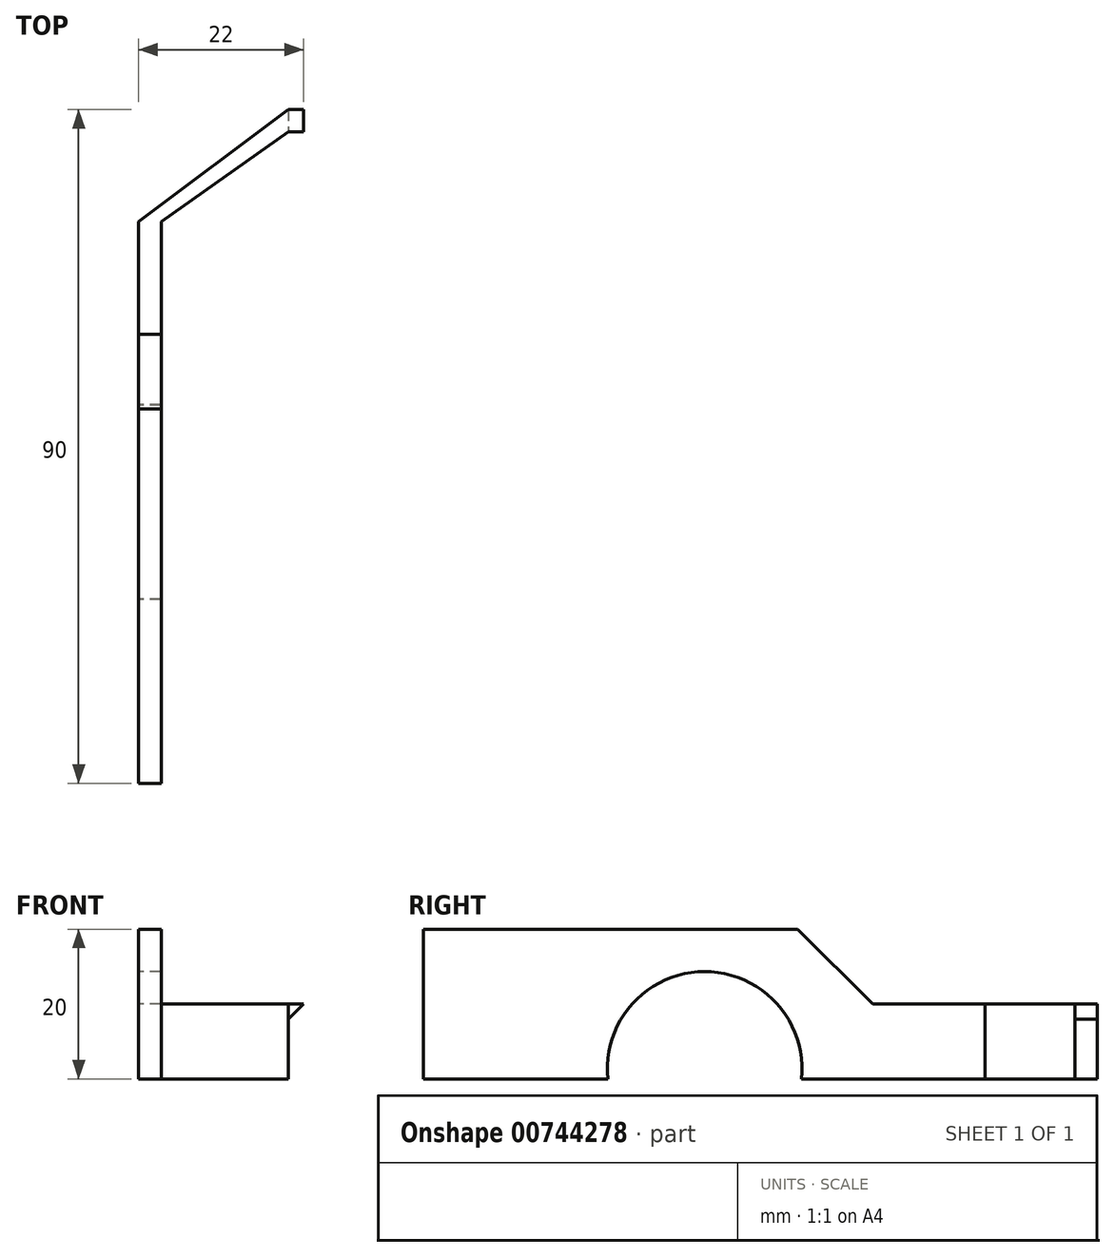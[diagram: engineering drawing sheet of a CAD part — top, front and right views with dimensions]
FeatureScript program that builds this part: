
annotation { "Feature Type Name" : "Feature", "Feature Type Description" : "" }
export const myFeature = defineFeature(function(context is Context, id is Id, definition is map)
    precondition{}
    {
        {
            var Q0;
            Q0=qCreatedBy(makeId("Top.planeOp"),FACE);
            var sketch = newSketch(context, id + "F0", { "sketchPlane" : qUnion([Q0])});
            skLineSegment(sketch, "E0", {"start": v(0, 0) * mm, "end": v(0, -3) * mm});
            skLineSegment(sketch, "E1", {"start": v(0, -3) * mm, "end": v(17, -15) * mm});
            skLineSegment(sketch, "E2", {"start": v(17, -15) * mm, "end": v(17, -90) * mm});
            skLineSegment(sketch, "E3", {"start": v(17, -90) * mm, "end": v(20, -90) * mm});
            skLineSegment(sketch, "E4", {"start": v(20, -90) * mm, "end": v(20, -15) * mm});
            skLineSegment(sketch, "E5", {"start": v(20, -15) * mm, "end": v(0, 0) * mm});
            skSolve(sketch);
        }
        {
            var Q0;
            Q0=qSketchRegion(id+"F0",true);
            extrude(context, id + "F1", {"entities" : qUnion([Q0]), "depth" : 10 * mm, "offsetDistance" : 25 * mm});
        }
        {
            var Q0;
            Q0=qCreatedBy(makeId("Front.planeOp"),FACE);
            var sketch = newSketch(context, id + "F2", { "sketchPlane" : qUnion([Q0])});
            skLineSegment(sketch, "E6", {"start": v(0, 10) * mm, "end": v(-2, 10) * mm});
            skLineSegment(sketch, "E7", {"start": v(-2, 10) * mm, "end": v(0, 8) * mm});
            skLineSegment(sketch, "E8", {"start": v(0, 8) * mm, "end": v(0, 10) * mm});
            skSolve(sketch);
        }
        {
            var Q0;
            Q0=qSketchRegion(id+"F2",true);
            extrude(context, id + "F3", {"entities" : qUnion([Q0]), "operationType" : NewBodyOperationType.ADD, "depth" : 3 * mm, "offsetDistance" : 25 * mm});
        }
        {
            var Q0;
            Q0=makeQuery(id+"F3.boolean.opBoolean","MERGE",FACE,{"derivedFrom":[makeQuery(id+"F1.opExtrude","CAP_FACE",FACE,{"disambiguationData":[OSD([sQuery(id+"F0.wireOp",EDGE,"E0"),sQuery(id+"F0.wireOp",EDGE,"E1"),sQuery(id+"F0.wireOp",EDGE,"E2"),sQuery(id+"F0.wireOp",EDGE,"E3"),sQuery(id+"F0.wireOp",EDGE,"E4"),sQuery(id+"F0.wireOp",EDGE,"E5")])],"isStart":false}),makeQuery(id+"F3.opExtrude","SWEPT_FACE",FACE,{"disambiguationData":[OSD([sQuery(id+"F2.wireOp",EDGE,"E6")])]})]});
            var sketch = newSketch(context, id + "F4", { "sketchPlane" : qUnion([Q0])});
            skLineSegment(sketch, "E9.bottom", {"start": v(17, -30) * mm, "end": v(20, -30) * mm});
            skLineSegment(sketch, "E9.top", {"start": v(17, -90) * mm, "end": v(20, -90) * mm});
            skLineSegment(sketch, "E9.left", {"start": v(17, -30) * mm, "end": v(17, -90) * mm});
            skLineSegment(sketch, "E9.right", {"start": v(20, -30) * mm, "end": v(20, -90) * mm});
            skSolve(sketch);
        }
        {
            var Q0;
            Q0=qSketchRegion(id+"F4",true);
            extrude(context, id + "F5", {"entities" : qUnion([Q0]), "operationType" : NewBodyOperationType.ADD, "depth" : 10 * mm, "offsetDistance" : 25 * mm});
        }
        {
            var Q0;
            Q0=makeQuery(id+"F5.opExtrude","CAP_EDGE",EDGE,{"disambiguationData":[OSD([sQuery(id+"F4.wireOp",EDGE,"E9.bottom")])],"isStart":false});
            chamfer(context, id + "F6", {"entities" : qUnion([Q0]), "width" : 10 * mm, "tangentPropagation" : true});
        }
        {
            var Q0;
            Q0=makeQuery(id+"F5.boolean.opBoolean","MERGE",FACE,{"derivedFrom":[makeQuery(id+"F1.opExtrude","SWEPT_FACE",FACE,{"disambiguationData":[OSD([sQuery(id+"F0.wireOp",EDGE,"E4")])]}),makeQuery(id+"F5.opExtrude","SWEPT_FACE",FACE,{"disambiguationData":[OSD([sQuery(id+"F4.wireOp",EDGE,"E9.right")])]})]});
            var sketch = newSketch(context, id + "F7", { "sketchPlane" : qUnion([Q0])});
            skArc(sketch, "E10", {"start": v(-39.5, 0) * mm, "mid": v(-52.43, 14.33) * mm, "end": v(-65.36, 0) * mm});
            skSolve(sketch);
        }
        {
            var Q0;
            {var subQ0=sQuery(id+"F7.wireOp",EDGE,"E10");Q0=makeQuery(id+"F7.imprint","IMPRINT",FACE,{"disambiguationData":[TD([[makeQuery(id+"F7.imprint","IMPRINT",EDGE,{"derivedFrom":subQ0}),1.0]])]});}
            extrude(context, id + "F8", {"entities" : qUnion([Q0]), "operationType" : NewBodyOperationType.REMOVE, "oppositeDirection" : true, "depth" : 25 * mm, "offsetDistance" : 25 * mm});
        }
        {
            var Q0;
            Q0=qCreatedBy(makeId("Right.planeOp"),FACE);
            cPlane(context, id + "F9", {"entities" : qUnion([Q0]), "cplaneType" : CPlaneType.OFFSET, "offset" : 2 * mm, "oppositeDirection" : true, "width" : 150 * mm, "height" : 150 * mm});
        }
        {
            var Q0;
            Q0=makeQuery(id+"F1.opExtrude","SWEPT_BODY",BODY,{"disambiguationData":[OSD([sQuery(id+"F0.wireOp",EDGE,"E0"),sQuery(id+"F0.wireOp",EDGE,"E1"),sQuery(id+"F0.wireOp",EDGE,"E2"),sQuery(id+"F0.wireOp",EDGE,"E3"),sQuery(id+"F0.wireOp",EDGE,"E4"),sQuery(id+"F0.wireOp",EDGE,"E5")])]});
            var Q1;
            Q1=qCreatedBy(id+"F9.planeOp",FACE);
            mirror(context, id + "F10", {"entities" : qUnion([Q0]), "mirrorPlane" : qUnion([Q1])});
        }
        {
            var Q0;
            Q0=makeQuery(id+"F1.opExtrude","SWEPT_BODY",BODY,{"disambiguationData":[OSD([sQuery(id+"F0.wireOp",EDGE,"E0"),sQuery(id+"F0.wireOp",EDGE,"E1"),sQuery(id+"F0.wireOp",EDGE,"E2"),sQuery(id+"F0.wireOp",EDGE,"E3"),sQuery(id+"F0.wireOp",EDGE,"E4"),sQuery(id+"F0.wireOp",EDGE,"E5")])]});
            deleteBodies(context, id + "F11", {"entities" : qUnion([Q0])});
        }
    });
